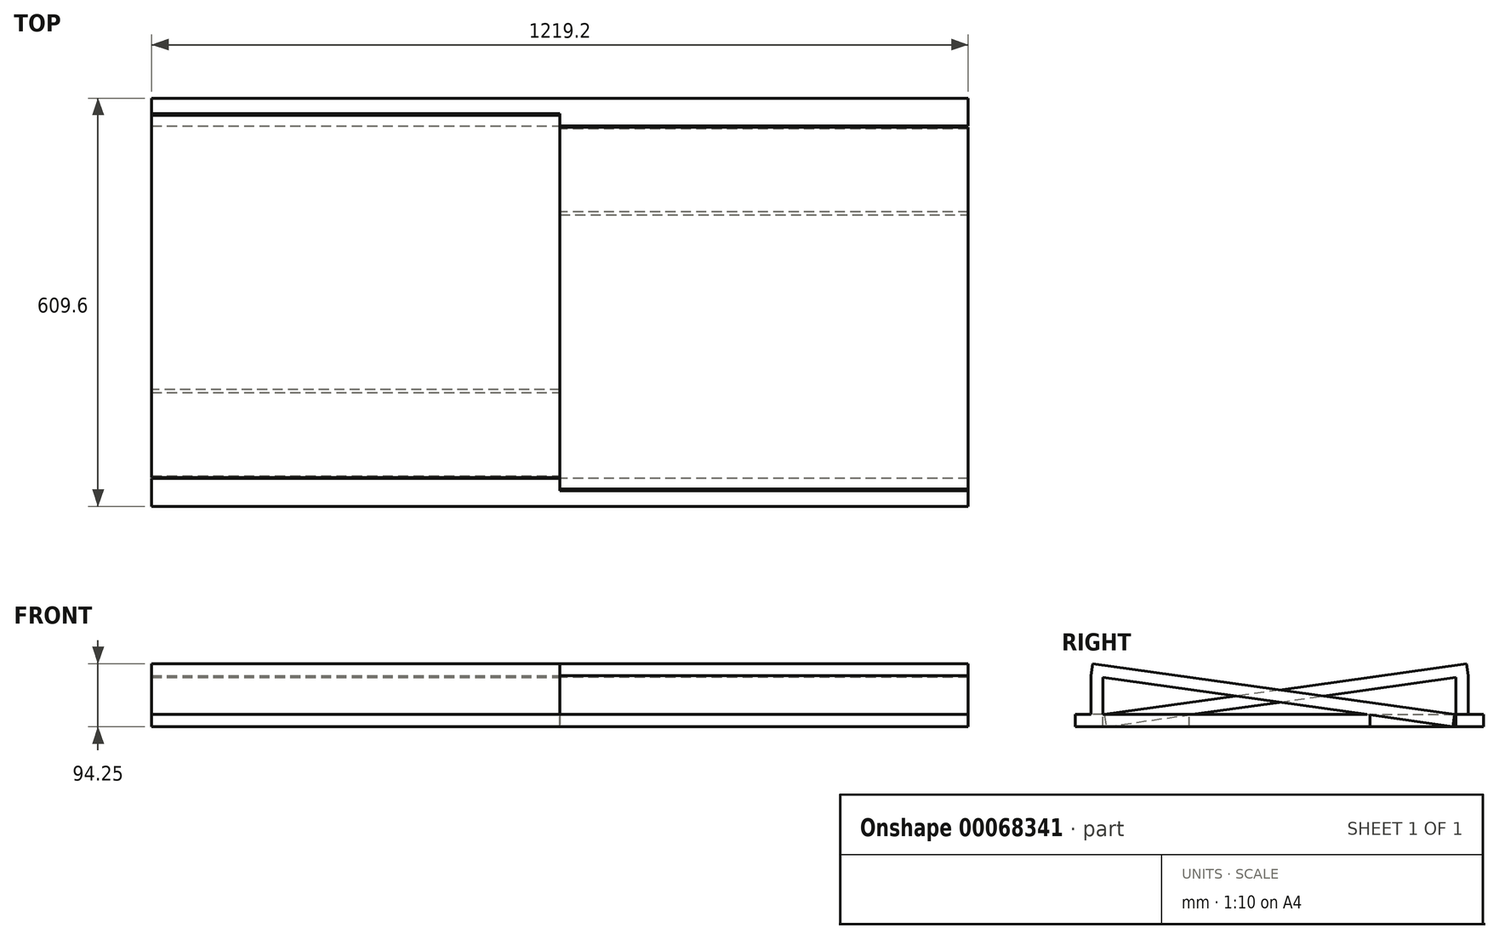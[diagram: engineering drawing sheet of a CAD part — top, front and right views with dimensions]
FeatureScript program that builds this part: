
annotation { "Feature Type Name" : "Feature", "Feature Type Description" : "" }
export const myFeature = defineFeature(function(context is Context, id is Id, definition is map)
    precondition{}
    {
        {
            var Q0;
            Q0=qCreatedBy(makeId("Top.planeOp"),FACE);
            var sketch = newSketch(context, id + "F0", { "sketchPlane" : qUnion([Q0])});
            skLineSegment(sketch, "E0.rect.bottom", {"start": v(609.6, 304.8) * mm, "end": v(-609.6, 304.8) * mm});
            skLineSegment(sketch, "E0.rect.top", {"start": v(609.6, -304.8) * mm, "end": v(-609.6, -304.8) * mm});
            skLineSegment(sketch, "E0.rect.left", {"start": v(609.6, 304.8) * mm, "end": v(609.6, -304.8) * mm});
            skLineSegment(sketch, "E0.rect.right", {"start": v(-609.6, 304.8) * mm, "end": v(-609.6, -304.8) * mm});
            skPoint(sketch, "E0.rect.middle", {"position": v(0, 0) * mm});
            skLineSegment(sketch, "E1", {"start": v(0, -304.8) * mm, "end": v(0, 304.8) * mm, "construction": true});
            skLineSegment(sketch, "E2.bottom", {"start": v(-609.6, -263.4) * mm, "end": v(0, -263.4) * mm});
            skLineSegment(sketch, "E2.top", {"start": v(-609.6, -134.87) * mm, "end": v(0, -134.87) * mm});
            skLineSegment(sketch, "E2.left", {"start": v(-609.6, -263.4) * mm, "end": v(-609.6, -134.87) * mm});
            skLineSegment(sketch, "E2.right", {"start": v(0, -263.4) * mm, "end": v(0, -134.87) * mm});
            skLineSegment(sketch, "E3.bottom", {"start": v(609.6, 263.4) * mm, "end": v(0, 263.4) * mm});
            skLineSegment(sketch, "E3.top", {"start": v(609.6, 134.87) * mm, "end": v(0, 134.87) * mm});
            skLineSegment(sketch, "E3.left", {"start": v(609.6, 263.4) * mm, "end": v(609.6, 134.87) * mm});
            skLineSegment(sketch, "E3.right", {"start": v(0, 263.4) * mm, "end": v(0, 134.87) * mm});
            skSolve(sketch);
        }
        {
            var Q0;
            {var subQ1=sQuery(id+"F0.wireOp",EDGE,"E0.rect.bottom");Q0=makeQuery(id+"F0.imprint","IMPRINT",FACE,{"disambiguationData":[TD([[makeQuery(id+"F0.imprint","IMPRINT",EDGE,{"derivedFrom":subQ1}),1.0]])]});}
            extrude(context, id + "F1", {"entities" : qUnion([Q0]), "oppositeDirection" : true, "depth" : 18.26 * mm});
        }
        {
            var Q0;
            Q0=qCreatedBy(makeId("Right.planeOp"),FACE);
            var sketch = newSketch(context, id + "F2", { "sketchPlane" : qUnion([Q0])});
            skLineSegment(sketch, "E4.bottom", {"start": v(263.4, 0) * mm, "end": v(281.65, 0) * mm});
            skLineSegment(sketch, "E4.left", {"start": v(263.4, 0) * mm, "end": v(263.4, 55.35) * mm});
            skLineSegment(sketch, "E4.right", {"start": v(281.65, 0) * mm, "end": v(281.65, 57.91) * mm});
            skLineSegment(sketch, "E5", {"start": v(281.65, 57.91) * mm, "end": v(263.4, 55.35) * mm});
            skLineSegment(sketch, "E6", {"start": v(281.65, 57.91) * mm, "end": v(279.11, 76) * mm});
            skLineSegment(sketch, "E7", {"start": v(279.11, 76) * mm, "end": v(-261.59, 0) * mm});
            skLineSegment(sketch, "E8", {"start": v(-261.59, 0) * mm, "end": v(-259.05, -18.08) * mm});
            skLineSegment(sketch, "E9", {"start": v(-259.05, -18.08) * mm, "end": v(263.4, 55.35) * mm});
            skLineSegment(sketch, "E10.MirrorCS", {"start": v(-279.11, 76) * mm, "end": v(261.59, 0) * mm});
            skLineSegment(sketch, "E11.MirrorCS", {"start": v(259.05, -18.08) * mm, "end": v(-263.4, 55.35) * mm});
            skLineSegment(sketch, "E12.MirrorCS", {"start": v(261.59, 0) * mm, "end": v(259.05, -18.08) * mm});
            skLineSegment(sketch, "E13.MirrorCS", {"start": v(-263.4, 0) * mm, "end": v(-263.4, 55.35) * mm});
            skLineSegment(sketch, "E14.MirrorCS", {"start": v(-281.65, 57.91) * mm, "end": v(-263.4, 55.35) * mm});
            skLineSegment(sketch, "E15.MirrorCS", {"start": v(-281.65, 0) * mm, "end": v(-281.65, 57.91) * mm});
            skLineSegment(sketch, "E16.MirrorCS", {"start": v(-263.4, 0) * mm, "end": v(-281.65, 0) * mm});
            skLineSegment(sketch, "E17.MirrorCS", {"start": v(-281.65, 57.91) * mm, "end": v(-279.11, 76) * mm});
            skSolve(sketch);
        }
        {
            var Q0;
            Q0=makeQuery(id+"F2.imprint","IMPRINT",FACE,{"disambiguationData":[TD([[makeQuery(id+"F2.imprint","IMPRINT",EDGE,{"derivedFrom":sQuery(id+"F2.wireOp",EDGE,"E5")}),-1.0]])]});
            var Q1;
            Q1=makeQuery(id+"F2.imprint","IMPRINT",FACE,{"disambiguationData":[TD([[makeQuery(id+"F2.imprint","IMPRINT",EDGE,{"derivedFrom":sQuery(id+"F2.wireOp",EDGE,"E4.bottom")}),1.0]])]});
            var Q2;
            {var subQ0=sQuery(id+"F2.wireOp",EDGE,"E10.MirrorCS");var subQ1=sQuery(id+"F2.wireOp",EDGE,"E7");var subQ2=makeQuery(id+"F2.imprint","INTERSECT",VERTEX,{"derivedFrom":[subQ1,subQ0]});Q2=makeQuery(id+"F2.imprint","IMPRINT",FACE,{"disambiguationData":[TD([[makeQuery(id+"F2.imprint","IMPRINT",EDGE,{"disambiguationData":[TD([[subQ2,-1.0]])],"derivedFrom":subQ1}),1.0]])]});}
            var Q3;
            {var subQ0=sQuery(id+"F2.wireOp",EDGE,"E8");Q3=makeQuery(id+"F2.imprint","IMPRINT",FACE,{"disambiguationData":[TD([[makeQuery(id+"F2.imprint","IMPRINT",EDGE,{"derivedFrom":subQ0}),1.0]])]});}
            var Q4;
            {var subQ0=sQuery(id+"F0.wireOp",EDGE,"E0.rect.right");Q4=makeQuery(id+"F1.opExtrude","SWEPT_FACE",FACE,{"disambiguationData":[OSD([subQ0]),TDD([makeQuery(id+"F0.imprint","IMPRINT",EDGE,{"disambiguationData":[TD([[makeQuery(id+"F0.imprint","INTERSECT",VERTEX,{"derivedFrom":[sQuery(id+"F0.wireOp",EDGE,"E0.rect.top"),subQ0]}),1.0]])],"derivedFrom":subQ0})])]});}
            extrude(context, id + "F3", {"entities" : qUnion([Q0, Q1, Q2, Q3]), "operationType" : NewBodyOperationType.ADD, "endBound" : BoundingType.UP_TO_SURFACE, "oppositeDirection" : true, "endBoundEntityFace" : qUnion([Q4]), "depth" : 25.4 * mm});
        }
        {
            var Q0;
            Q0=makeQuery(id+"F2.imprint","IMPRINT",FACE,{"disambiguationData":[TD([[makeQuery(id+"F2.imprint","IMPRINT",EDGE,{"derivedFrom":sQuery(id+"F2.wireOp",EDGE,"E13.MirrorCS")}),1.0]])]});
            var Q1;
            {var subQ0=sQuery(id+"F2.wireOp",EDGE,"E14.MirrorCS");Q1=makeQuery(id+"F2.imprint","IMPRINT",FACE,{"disambiguationData":[TD([[makeQuery(id+"F2.imprint","IMPRINT",EDGE,{"derivedFrom":subQ0}),1.0]])]});}
            var Q2;
            {var subQ0=sQuery(id+"F2.wireOp",EDGE,"E10.MirrorCS");var subQ1=sQuery(id+"F2.wireOp",EDGE,"E7");var subQ2=makeQuery(id+"F2.imprint","INTERSECT",VERTEX,{"derivedFrom":[subQ1,subQ0]});Q2=makeQuery(id+"F2.imprint","IMPRINT",FACE,{"disambiguationData":[TD([[makeQuery(id+"F2.imprint","IMPRINT",EDGE,{"disambiguationData":[TD([[subQ2,-1.0]])],"derivedFrom":subQ1}),1.0]])]});}
            var Q3;
            {var subQ5=sQuery(id+"F2.wireOp",EDGE,"E12.MirrorCS");Q3=makeQuery(id+"F2.imprint","IMPRINT",FACE,{"disambiguationData":[TD([[makeQuery(id+"F2.imprint","IMPRINT",EDGE,{"derivedFrom":subQ5}),-1.0]])]});}
            var Q4;
            {var subQ0=sQuery(id+"F0.wireOp",EDGE,"E0.rect.left");Q4=makeQuery(id+"F1.opExtrude","SWEPT_FACE",FACE,{"disambiguationData":[OSD([subQ0]),TDD([makeQuery(id+"F0.imprint","IMPRINT",EDGE,{"disambiguationData":[TD([[makeQuery(id+"F0.imprint","INTERSECT",VERTEX,{"derivedFrom":[sQuery(id+"F0.wireOp",EDGE,"E0.rect.top"),subQ0]}),1.0]])],"derivedFrom":subQ0})])]});}
            extrude(context, id + "F4", {"entities" : qUnion([Q0, Q1, Q2, Q3]), "operationType" : NewBodyOperationType.ADD, "endBound" : BoundingType.UP_TO_SURFACE, "endBoundEntityFace" : qUnion([Q4]), "depth" : 25.4 * mm});
        }
    });
